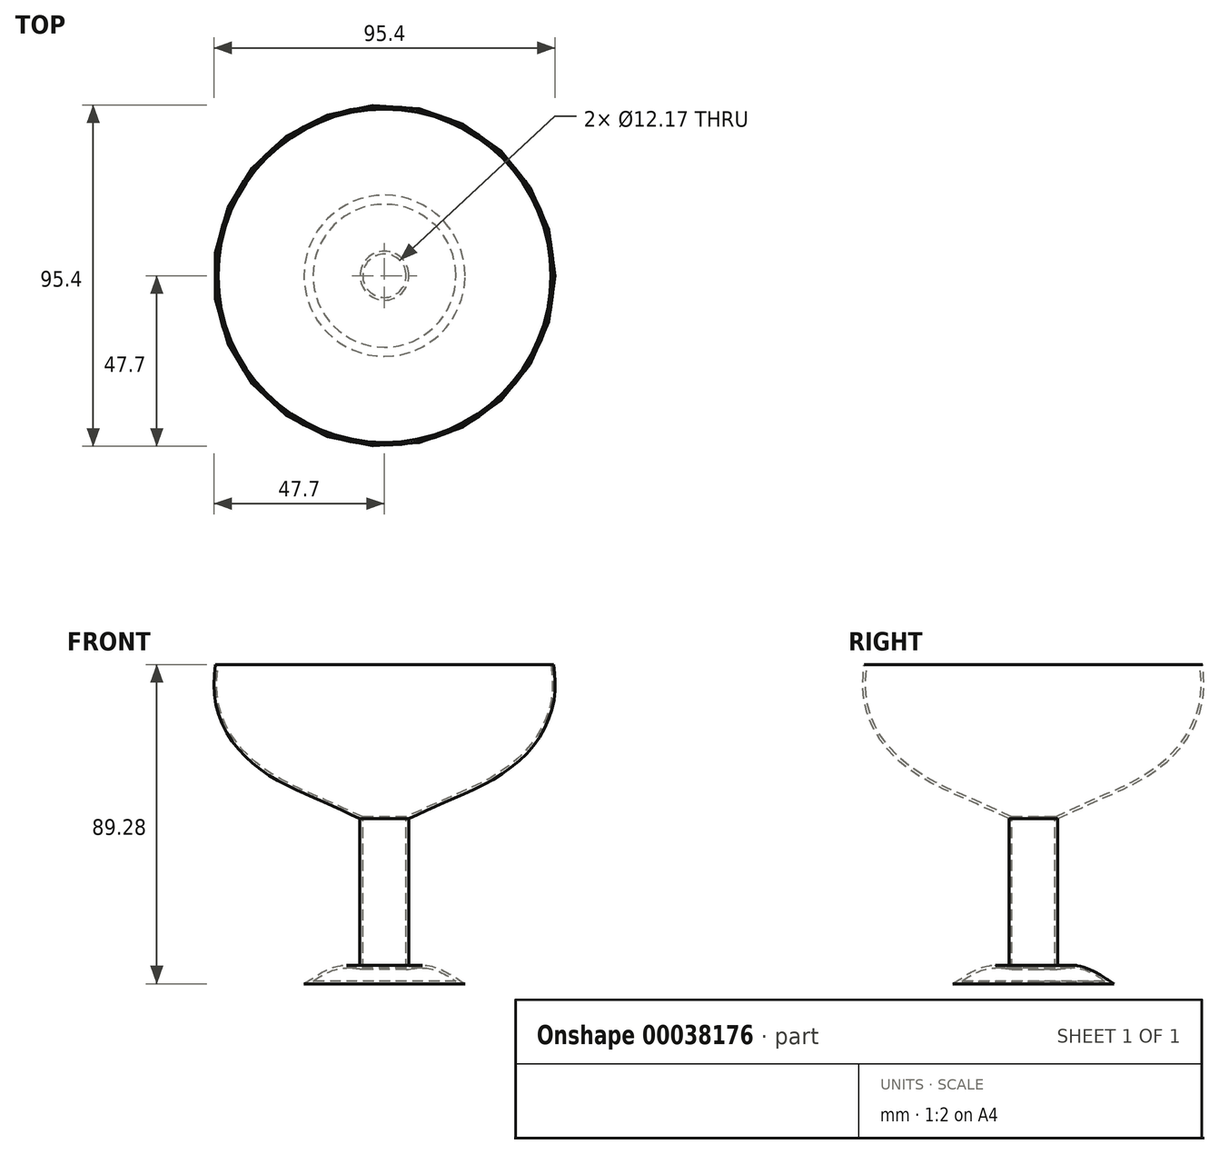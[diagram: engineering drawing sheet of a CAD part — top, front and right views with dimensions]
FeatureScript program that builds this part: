
annotation { "Feature Type Name" : "Feature", "Feature Type Description" : "" }
export const myFeature = defineFeature(function(context is Context, id is Id, definition is map)
    precondition{}
    {
        {
            var Q0;
            Q0=qCreatedBy(makeId("Front.planeOp"),FACE);
            var sketch = newSketch(context, id + "F0", { "sketchPlane" : qUnion([Q0])});
            skLineSegment(sketch, "E0", {"start": v(0, 45.78) * mm, "end": v(0, -43.5) * mm});
            skLineSegment(sketch, "E1", {"start": v(0, -43.5) * mm, "end": v(22.53, -43.5) * mm});
            skLineSegment(sketch, "E2", {"start": v(6.85, 2.7) * mm, "end": v(6.85, -38.65) * mm});
            skLineSegment(sketch, "E3", {"start": v(0, 45.78) * mm, "end": v(47.35, 45.78) * mm});
            skFitSpline(sketch, "E4", {"points": [v(47.35, 45.78) * mm, v(47.35, 35.51) * mm, v(42.22, 23.82) * mm, v(31.66, 14.4) * mm, v(18.26, 7.84) * mm, v(6.85, 2.7) * mm], "startDerivative": vector(5.14, -56.5) * mm, "endDerivative": vector(-56.25, -25.64) * mm});
            skFitSpline(sketch, "E5", {"points": [v(6.85, -38.65) * mm, v(13.4, -38.65) * mm, v(22.53, -43.5) * mm], "startDerivative": vector(14.44, 1.93) * mm, "endDerivative": vector(16.85, -11.14) * mm});
            skSolve(sketch);
        }
        {
            var Q0;
            Q0=makeQuery(id+"F0.imprint","IMPRINT",FACE,{"disambiguationData":[TD([[makeQuery(id+"F0.imprint","IMPRINT",EDGE,{"derivedFrom":sQuery(id+"F0.wireOp",EDGE,"E0")}),1.0]])]});
            var Q1;
            Q1=sQuery(id+"F0.wireOp",EDGE,"E0");
            revolve(context, id + "F1", {"entities" : qUnion([Q0]), "axis" : qUnion([Q1]), "revolveType" : RevolveType.FULL});
        }
        {
            var Q0;
            Q0=makeQuery(id+"F1.opRevolve","SWEPT_FACE",FACE,{"disambiguationData":[OSD([sQuery(id+"F0.wireOp",EDGE,"E3")])]});
            shell(context, id + "F2", {"entities" : qUnion([Q0]), "thickness" : 0.76 * mm});
        }
    });
